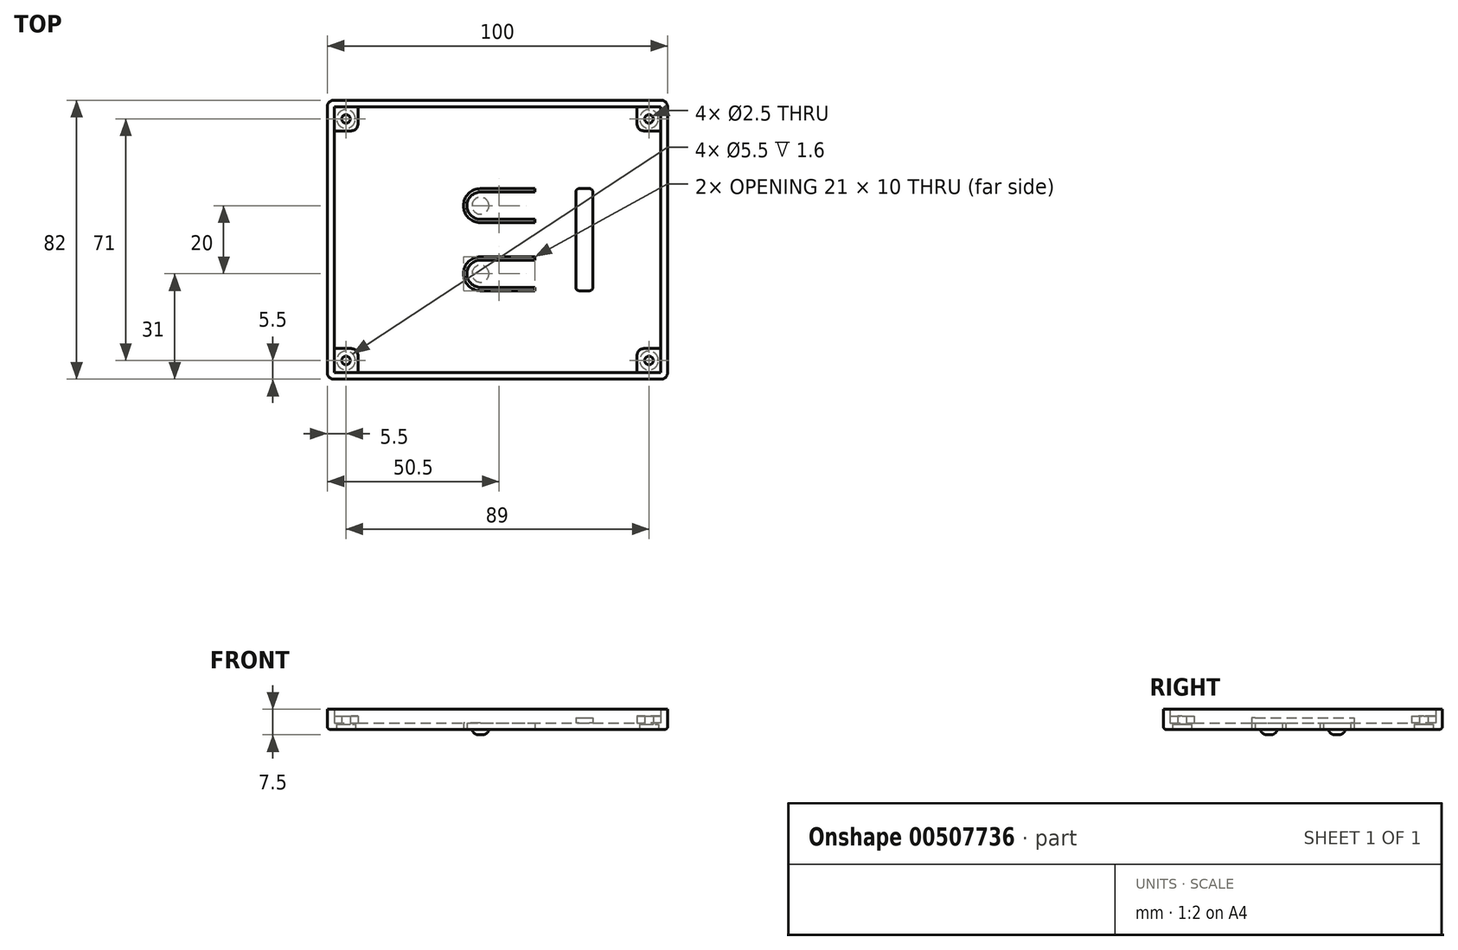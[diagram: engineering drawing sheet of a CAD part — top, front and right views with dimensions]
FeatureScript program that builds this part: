
annotation { "Feature Type Name" : "Feature", "Feature Type Description" : "" }
export const myFeature = defineFeature(function(context is Context, id is Id, definition is map)
    precondition{}
    {
        {
            var Q0;
            Q0=qCreatedBy(makeId("Top.planeOp"),FACE);
            var sketch = newSketch(context, id + "F0", { "sketchPlane" : qUnion([Q0])});
            skLineSegment(sketch, "E0.bottom", {"start": v(2, 0) * mm, "end": v(98, 0) * mm});
            skLineSegment(sketch, "E0.top", {"start": v(2, 82) * mm, "end": v(98, 82) * mm});
            skLineSegment(sketch, "E0.left", {"start": v(0, 2) * mm, "end": v(0, 80) * mm});
            skLineSegment(sketch, "E0.right", {"start": v(100, 2) * mm, "end": v(100, 80) * mm});
            skPoint(sketch, "E1.visualSharp", {"position": v(0, 82) * mm});
            skArc(sketch, "E1.filletArc", {"start": v(2, 82) * mm, "mid": v(0.59, 81.41) * mm, "end": v(0, 80) * mm});
            skPoint(sketch, "E2.visualSharp", {"position": v(0, 0) * mm});
            skArc(sketch, "E2.filletArc", {"start": v(0, 2) * mm, "mid": v(0.59, 0.59) * mm, "end": v(2, 0) * mm});
            skPoint(sketch, "E3.visualSharp", {"position": v(100, 0) * mm});
            skArc(sketch, "E3.filletArc", {"start": v(98, 0) * mm, "mid": v(99.41, 0.59) * mm, "end": v(100, 2) * mm});
            skPoint(sketch, "E4.visualSharp", {"position": v(100, 82) * mm});
            skArc(sketch, "E4.filletArc", {"start": v(100, 80) * mm, "mid": v(99.41, 81.41) * mm, "end": v(98, 82) * mm});
            skSolve(sketch);
        }
        {
            var Q0;
            Q0=makeQuery(id+"F0.imprint","IMPRINT",FACE,{"disambiguationData":[TD([[makeQuery(id+"F0.imprint","IMPRINT",EDGE,{"derivedFrom":sQuery(id+"F0.wireOp",EDGE,"E0.bottom")}),1.0]])]});
            extrude(context, id + "F1", {"entities" : qUnion([Q0]), "depth" : 2 * mm, "offsetDistance" : 25 * mm});
        }
        {
            var Q0;
            Q0=makeQuery(id+"F1.opExtrude","CAP_FACE",FACE,{"disambiguationData":[OSD([sQuery(id+"F0.wireOp",EDGE,"E0.bottom"),sQuery(id+"F0.wireOp",EDGE,"E0.top"),sQuery(id+"F0.wireOp",EDGE,"E0.left"),sQuery(id+"F0.wireOp",EDGE,"E0.right"),sQuery(id+"F0.wireOp",EDGE,"E1.filletArc"),sQuery(id+"F0.wireOp",EDGE,"E2.filletArc"),sQuery(id+"F0.wireOp",EDGE,"E3.filletArc"),sQuery(id+"F0.wireOp",EDGE,"E4.filletArc")])],"isStart":false});
            var sketch = newSketch(context, id + "F2", { "sketchPlane" : qUnion([Q0])});
            skLineSegment(sketch, "E5.0", {"start": v(2, 80) * mm, "end": v(98, 80) * mm});
            skLineSegment(sketch, "E5.1", {"start": v(98, 80) * mm, "end": v(98, 80) * mm});
            skLineSegment(sketch, "E5.2", {"start": v(2, 80) * mm, "end": v(2, 80) * mm});
            skLineSegment(sketch, "E5.3", {"start": v(98, 2) * mm, "end": v(98, 80) * mm});
            skLineSegment(sketch, "E5.4", {"start": v(2, 2) * mm, "end": v(2, 80) * mm});
            skLineSegment(sketch, "E5.5", {"start": v(2, 2) * mm, "end": v(2, 2) * mm});
            skLineSegment(sketch, "E5.6", {"start": v(2, 2) * mm, "end": v(98, 2) * mm});
            skLineSegment(sketch, "E5.7", {"start": v(98, 2) * mm, "end": v(98, 2) * mm});
            skSolve(sketch);
        }
        {
            var Q0;
            Q0=makeQuery(id+"F2.imprint","IMPRINT",FACE,{"disambiguationData":[TD([[makeQuery(id+"F2.imprint","IMPRINT",EDGE,{"derivedFrom":sQuery(id+"F2.wireOp",EDGE,"E5.0")}),1.0]])]});
            extrude(context, id + "F3", {"entities" : qUnion([Q0]), "operationType" : NewBodyOperationType.ADD, "depth" : 4 * mm, "offsetDistance" : 25 * mm});
        }
        {
            var Q0;
            Q0=makeQuery(id+"F1.opExtrude","CAP_FACE",FACE,{"disambiguationData":[OSD([sQuery(id+"F0.wireOp",EDGE,"E0.bottom"),sQuery(id+"F0.wireOp",EDGE,"E0.top"),sQuery(id+"F0.wireOp",EDGE,"E0.left"),sQuery(id+"F0.wireOp",EDGE,"E0.right"),sQuery(id+"F0.wireOp",EDGE,"E1.filletArc"),sQuery(id+"F0.wireOp",EDGE,"E2.filletArc"),sQuery(id+"F0.wireOp",EDGE,"E3.filletArc"),sQuery(id+"F0.wireOp",EDGE,"E4.filletArc")])],"isStart":false});
            var sketch = newSketch(context, id + "F4", { "sketchPlane" : qUnion([Q0])});
            skLineSegment(sketch, "E6.bottom", {"start": v(2, 2) * mm, "end": v(9, 2) * mm});
            skLineSegment(sketch, "E6.top", {"start": v(2, 9) * mm, "end": v(7, 9) * mm});
            skLineSegment(sketch, "E6.left", {"start": v(2, 2) * mm, "end": v(2, 9) * mm});
            skLineSegment(sketch, "E6.right", {"start": v(9, 2) * mm, "end": v(9, 7) * mm});
            skLineSegment(sketch, "E7.bottom", {"start": v(2, 80) * mm, "end": v(9, 80) * mm});
            skLineSegment(sketch, "E7.top", {"start": v(2, 73) * mm, "end": v(7, 73) * mm});
            skLineSegment(sketch, "E7.left", {"start": v(2, 80) * mm, "end": v(2, 73) * mm});
            skLineSegment(sketch, "E7.right", {"start": v(9, 80) * mm, "end": v(9, 75) * mm});
            skLineSegment(sketch, "E8.bottom", {"start": v(98, 2) * mm, "end": v(91, 2) * mm});
            skLineSegment(sketch, "E8.top", {"start": v(98, 9) * mm, "end": v(93, 9) * mm});
            skLineSegment(sketch, "E8.left", {"start": v(98, 2) * mm, "end": v(98, 9) * mm});
            skLineSegment(sketch, "E8.right", {"start": v(91, 2) * mm, "end": v(91, 7) * mm});
            skLineSegment(sketch, "E9.bottom", {"start": v(98, 80) * mm, "end": v(91, 80) * mm});
            skLineSegment(sketch, "E9.top", {"start": v(98, 73) * mm, "end": v(93, 73) * mm});
            skLineSegment(sketch, "E9.left", {"start": v(98, 80) * mm, "end": v(98, 73) * mm});
            skLineSegment(sketch, "E9.right", {"start": v(91, 80) * mm, "end": v(91, 75) * mm});
            skPoint(sketch, "E10.visualSharp", {"position": v(9, 9) * mm});
            skArc(sketch, "E10.filletArc", {"start": v(9, 7) * mm, "mid": v(8.41, 8.41) * mm, "end": v(7, 9) * mm});
            skPoint(sketch, "E11.visualSharp", {"position": v(9, 73) * mm});
            skArc(sketch, "E11.filletArc", {"start": v(7, 73) * mm, "mid": v(8.41, 73.59) * mm, "end": v(9, 75) * mm});
            skPoint(sketch, "E12.visualSharp", {"position": v(91, 73) * mm});
            skArc(sketch, "E12.filletArc", {"start": v(91, 75) * mm, "mid": v(91.59, 73.59) * mm, "end": v(93, 73) * mm});
            skPoint(sketch, "E13.visualSharp", {"position": v(91, 9) * mm});
            skArc(sketch, "E13.filletArc", {"start": v(93, 9) * mm, "mid": v(91.59, 8.41) * mm, "end": v(91, 7) * mm});
            skSolve(sketch);
        }
        {
            var Q0;
            Q0=qSketchRegion(id+"F4",true);
            extrude(context, id + "F5", {"entities" : qUnion([Q0]), "operationType" : NewBodyOperationType.ADD, "depth" : 2 * mm, "offsetDistance" : 25 * mm});
        }
        {
            var Q0;
            Q0=makeQuery(id+"F1.opExtrude","CAP_FACE",FACE,{"disambiguationData":[OSD([sQuery(id+"F0.wireOp",EDGE,"E0.bottom"),sQuery(id+"F0.wireOp",EDGE,"E0.top"),sQuery(id+"F0.wireOp",EDGE,"E0.left"),sQuery(id+"F0.wireOp",EDGE,"E0.right"),sQuery(id+"F0.wireOp",EDGE,"E1.filletArc"),sQuery(id+"F0.wireOp",EDGE,"E2.filletArc"),sQuery(id+"F0.wireOp",EDGE,"E3.filletArc"),sQuery(id+"F0.wireOp",EDGE,"E4.filletArc")])],"isStart":true});
            var sketch = newSketch(context, id + "F6", { "sketchPlane" : qUnion([Q0])});
            skCircle(sketch, "E14", {"center": v(94.5, -5.5) * mm, "radius": 1.25 * mm});
            skCircle(sketch, "E15", {"center": v(94.5, -76.5) * mm, "radius": 1.25 * mm});
            skCircle(sketch, "E16", {"center": v(5.5, -76.5) * mm, "radius": 1.25 * mm});
            skCircle(sketch, "E17", {"center": v(5.5, -5.5) * mm, "radius": 1.25 * mm});
            skSolve(sketch);
        }
        {
            var Q0;
            Q0=qSketchRegion(id+"F6",true);
            extrude(context, id + "F7", {"entities" : qUnion([Q0]), "operationType" : NewBodyOperationType.REMOVE, "oppositeDirection" : true, "depth" : 6 * mm, "offsetDistance" : 25 * mm});
        }
        {
            var Q0;
            Q0=makeQuery(id+"F1.opExtrude","CAP_FACE",FACE,{"disambiguationData":[OSD([sQuery(id+"F0.wireOp",EDGE,"E0.bottom"),sQuery(id+"F0.wireOp",EDGE,"E0.top"),sQuery(id+"F0.wireOp",EDGE,"E0.left"),sQuery(id+"F0.wireOp",EDGE,"E0.right"),sQuery(id+"F0.wireOp",EDGE,"E1.filletArc"),sQuery(id+"F0.wireOp",EDGE,"E2.filletArc"),sQuery(id+"F0.wireOp",EDGE,"E3.filletArc"),sQuery(id+"F0.wireOp",EDGE,"E4.filletArc")])],"isStart":true});
            var sketch = newSketch(context, id + "F8", { "sketchPlane" : qUnion([Q0])});
            skCircle(sketch, "E18", {"center": v(5.5, -76.5) * mm, "radius": 2.75 * mm});
            skCircle(sketch, "E19", {"center": v(5.5, -5.5) * mm, "radius": 2.75 * mm});
            skCircle(sketch, "E20", {"center": v(94.5, -5.5) * mm, "radius": 2.75 * mm});
            skCircle(sketch, "E21", {"center": v(94.5, -76.5) * mm, "radius": 2.75 * mm});
            skSolve(sketch);
        }
        {
            var Q0;
            Q0=qSketchRegion(id+"F8",true);
            extrude(context, id + "F9", {"entities" : qUnion([Q0]), "operationType" : NewBodyOperationType.REMOVE, "oppositeDirection" : true, "depth" : 1.6 * mm, "offsetDistance" : 25 * mm});
        }
        {
            var Q0;
            Q0=makeQuery(id+"F1.opExtrude","CAP_FACE",FACE,{"disambiguationData":[OSD([sQuery(id+"F0.wireOp",EDGE,"E0.bottom"),sQuery(id+"F0.wireOp",EDGE,"E0.top"),sQuery(id+"F0.wireOp",EDGE,"E0.left"),sQuery(id+"F0.wireOp",EDGE,"E0.right"),sQuery(id+"F0.wireOp",EDGE,"E1.filletArc"),sQuery(id+"F0.wireOp",EDGE,"E2.filletArc"),sQuery(id+"F0.wireOp",EDGE,"E3.filletArc"),sQuery(id+"F0.wireOp",EDGE,"E4.filletArc")])],"isStart":false});
            var sketch = newSketch(context, id + "F10", { "sketchPlane" : qUnion([Q0])});
            skLineSegment(sketch, "E22.bottom", {"start": v(74, 26) * mm, "end": v(77, 26) * mm});
            skLineSegment(sketch, "E22.top", {"start": v(74, 56) * mm, "end": v(77, 56) * mm});
            skLineSegment(sketch, "E22.left", {"start": v(73, 27) * mm, "end": v(73, 55) * mm});
            skLineSegment(sketch, "E22.right", {"start": v(78, 27) * mm, "end": v(78, 55) * mm});
            skPoint(sketch, "E23.visualSharp", {"position": v(78, 26) * mm});
            skArc(sketch, "E23.filletArc", {"start": v(77, 26) * mm, "mid": v(77.7, 26.3) * mm, "end": v(78, 27) * mm});
            skPoint(sketch, "E24.visualSharp", {"position": v(73, 26) * mm});
            skArc(sketch, "E24.filletArc", {"start": v(73, 27) * mm, "mid": v(73.3, 26.3) * mm, "end": v(74, 26) * mm});
            skPoint(sketch, "E25.visualSharp", {"position": v(73, 56) * mm});
            skArc(sketch, "E25.filletArc", {"start": v(74, 56) * mm, "mid": v(73.3, 55.7) * mm, "end": v(73, 55) * mm});
            skPoint(sketch, "E26.visualSharp", {"position": v(78, 56) * mm});
            skArc(sketch, "E26.filletArc", {"start": v(78, 55) * mm, "mid": v(77.7, 55.7) * mm, "end": v(77, 56) * mm});
            skSolve(sketch);
        }
        {
            var Q0;
            Q0=makeQuery(id+"F1.opExtrude","CAP_EDGE",EDGE,{"disambiguationData":[OSD([sQuery(id+"F0.wireOp",EDGE,"E0.top")])],"isStart":true});
            fillet(context, id + "F11", {"entities" : qUnion([Q0]), "radius" : 1 * mm, "tangentPropagation" : true, "allowEdgeOverflow" : false});
        }
        {
            var Q0;
            Q0=makeQuery(id+"F1.opExtrude","CAP_FACE",FACE,{"disambiguationData":[OSD([sQuery(id+"F0.wireOp",EDGE,"E0.bottom"),sQuery(id+"F0.wireOp",EDGE,"E0.top"),sQuery(id+"F0.wireOp",EDGE,"E0.left"),sQuery(id+"F0.wireOp",EDGE,"E0.right"),sQuery(id+"F0.wireOp",EDGE,"E1.filletArc"),sQuery(id+"F0.wireOp",EDGE,"E2.filletArc"),sQuery(id+"F0.wireOp",EDGE,"E3.filletArc"),sQuery(id+"F0.wireOp",EDGE,"E4.filletArc")])],"isStart":true});
            var sketch = newSketch(context, id + "F12", { "sketchPlane" : qUnion([Q0])});
            skLineSegment(sketch, "E27.bottom", {"start": v(45, -26) * mm, "end": v(61, -26) * mm});
            skLineSegment(sketch, "E27.top", {"start": v(45, -36) * mm, "end": v(61, -36) * mm});
            skLineSegment(sketch, "E27.right", {"start": v(61, -26) * mm, "end": v(61, -27) * mm});
            skArc(sketch, "E28.filletArc", {"start": v(45, -26) * mm, "mid": v(41.46, -27.46) * mm, "end": v(40, -31) * mm});
            skArc(sketch, "E29.filletArc", {"start": v(40, -31) * mm, "mid": v(41.46, -34.54) * mm, "end": v(45, -36) * mm});
            skLineSegment(sketch, "E30.0", {"start": v(45, -27) * mm, "end": v(61, -27) * mm});
            skArc(sketch, "E30.1", {"start": v(45, -27) * mm, "mid": v(42.17, -28.17) * mm, "end": v(41, -31) * mm});
            skArc(sketch, "E30.2", {"start": v(41, -31) * mm, "mid": v(42.17, -33.83) * mm, "end": v(45, -35) * mm});
            skLineSegment(sketch, "E30.3", {"start": v(45, -35) * mm, "end": v(61, -35) * mm});
            skLineSegment(sketch, "E31.trimOffspring", {"start": v(61, -35) * mm, "end": v(61, -36) * mm});
            skCircle(sketch, "E32", {"center": v(45, -31) * mm, "radius": 2.5 * mm});
            skLineSegment(sketch, "E33.bottom", {"start": v(45, -46) * mm, "end": v(61, -46) * mm});
            skLineSegment(sketch, "E33.top", {"start": v(45, -56) * mm, "end": v(61, -56) * mm});
            skLineSegment(sketch, "E33.right", {"start": v(61, -46) * mm, "end": v(61, -47) * mm});
            skArc(sketch, "E34.filletArc", {"start": v(45, -46) * mm, "mid": v(41.46, -47.46) * mm, "end": v(40, -51) * mm});
            skArc(sketch, "E35.filletArc", {"start": v(40, -51) * mm, "mid": v(41.46, -54.54) * mm, "end": v(45, -56) * mm});
            skLineSegment(sketch, "E36.0", {"start": v(45, -47) * mm, "end": v(61, -47) * mm});
            skArc(sketch, "E36.1", {"start": v(45, -47) * mm, "mid": v(42.17, -48.17) * mm, "end": v(41, -51) * mm});
            skArc(sketch, "E36.2", {"start": v(41, -51) * mm, "mid": v(42.17, -53.83) * mm, "end": v(45, -55) * mm});
            skLineSegment(sketch, "E36.3", {"start": v(45, -55) * mm, "end": v(61, -55) * mm});
            skLineSegment(sketch, "E37.trimOffspring", {"start": v(61, -55) * mm, "end": v(61, -56) * mm});
            skCircle(sketch, "E38", {"center": v(45, -51) * mm, "radius": 2.5 * mm});
            skSolve(sketch);
        }
        {
            var Q0;
            Q0=makeQuery(id+"F12.imprint","IMPRINT",FACE,{"disambiguationData":[TD([[makeQuery(id+"F12.imprint","IMPRINT",EDGE,{"derivedFrom":sQuery(id+"F12.wireOp",EDGE,"E27.bottom")}),-1.0]])]});
            var Q1;
            Q1=makeQuery(id+"F12.imprint","IMPRINT",FACE,{"disambiguationData":[TD([[makeQuery(id+"F12.imprint","IMPRINT",EDGE,{"derivedFrom":sQuery(id+"F12.wireOp",EDGE,"E33.bottom")}),-1.0]])]});
            extrude(context, id + "F13", {"entities" : qUnion([Q0, Q1]), "operationType" : NewBodyOperationType.REMOVE, "oppositeDirection" : true, "depth" : 2 * mm, "offsetDistance" : 25 * mm});
        }
        {
            var Q0;
            Q0=makeQuery(id+"F12.imprint","IMPRINT",FACE,{"disambiguationData":[TD([[makeQuery(id+"F12.imprint","IMPRINT",EDGE,{"derivedFrom":sQuery(id+"F12.wireOp",EDGE,"E38")}),1.0]])]});
            var Q1;
            Q1=makeQuery(id+"F12.imprint","IMPRINT",FACE,{"disambiguationData":[TD([[makeQuery(id+"F12.imprint","IMPRINT",EDGE,{"derivedFrom":sQuery(id+"F12.wireOp",EDGE,"E32")}),1.0]])]});
            extrude(context, id + "F14", {"entities" : qUnion([Q0, Q1]), "operationType" : NewBodyOperationType.ADD, "depth" : 1.5 * mm, "offsetDistance" : 25 * mm});
        }
        {
            var Q0;
            Q0=makeQuery(id+"F14.opExtrude","CAP_EDGE",EDGE,{"disambiguationData":[OSD([sQuery(id+"F12.wireOp",EDGE,"E38")])],"isStart":false});
            var Q1;
            Q1=makeQuery(id+"F14.opExtrude","CAP_EDGE",EDGE,{"disambiguationData":[OSD([sQuery(id+"F12.wireOp",EDGE,"E32")])],"isStart":false});
            fillet(context, id + "F15", {"entities" : qUnion([Q0, Q1]), "radius" : 2 * mm, "tangentPropagation" : true, "allowEdgeOverflow" : false});
        }
        {
            var Q0;
            Q0=makeQuery(id+"F10.imprint","IMPRINT",FACE,{"disambiguationData":[TD([[makeQuery(id+"F10.imprint","IMPRINT",EDGE,{"derivedFrom":sQuery(id+"F10.wireOp",EDGE,"E22.bottom")}),1.0]])]});
            extrude(context, id + "F16", {"entities" : qUnion([Q0]), "operationType" : NewBodyOperationType.ADD, "depth" : 1.5 * mm, "offsetDistance" : 25 * mm});
        }
    });
